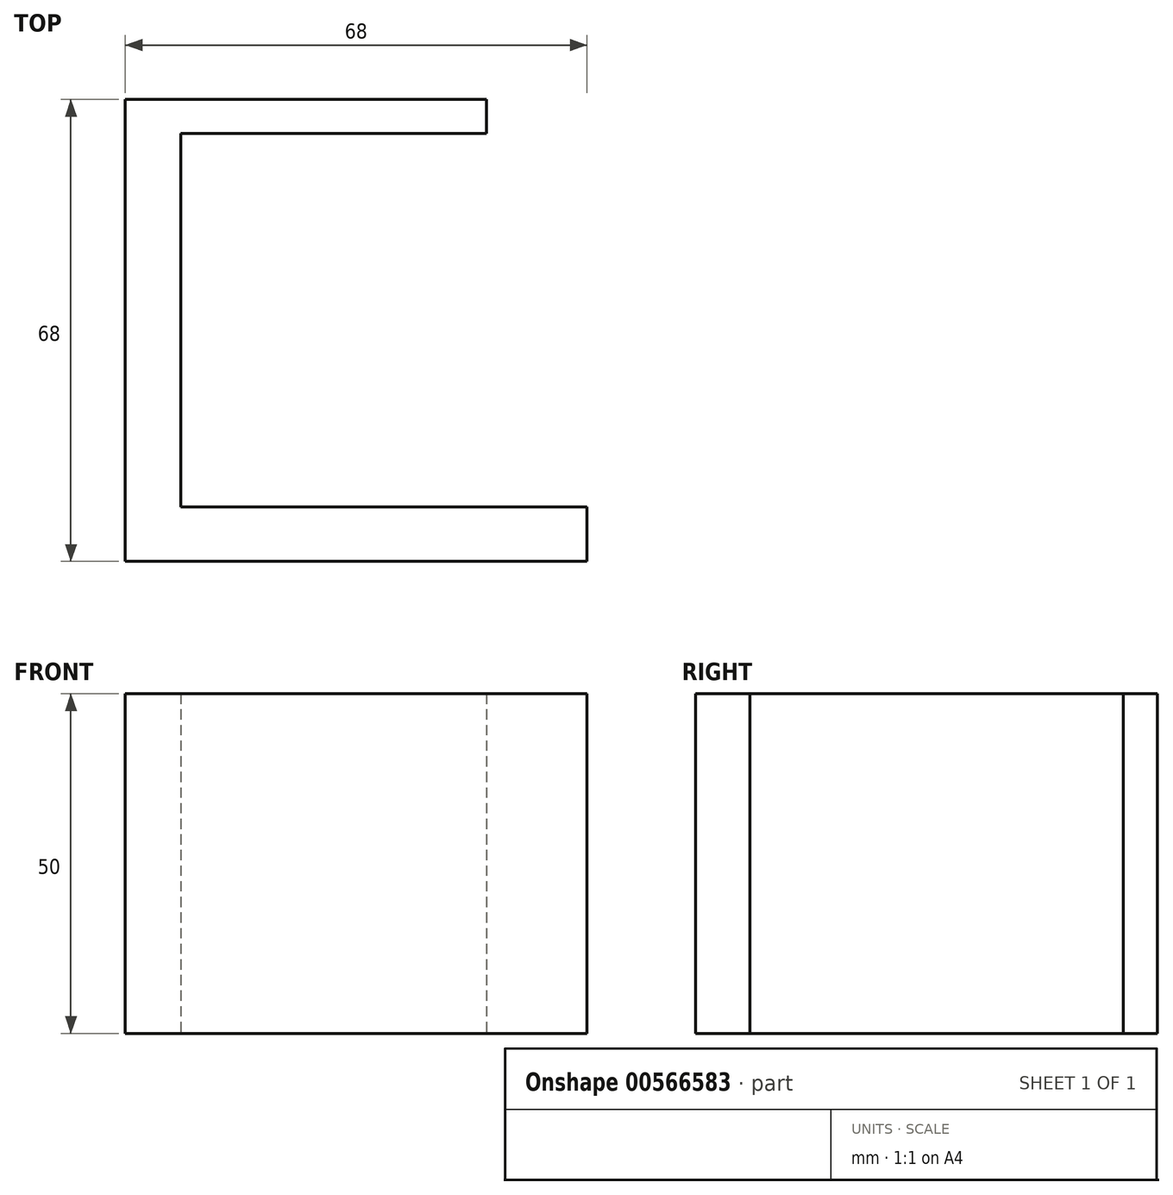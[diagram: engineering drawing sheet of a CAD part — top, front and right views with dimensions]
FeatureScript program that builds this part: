
annotation { "Feature Type Name" : "Feature", "Feature Type Description" : "" }
export const myFeature = defineFeature(function(context is Context, id is Id, definition is map)
    precondition{}
    {
        {
            var Q0;
            Q0=qCreatedBy(makeId("Top.planeOp"),FACE);
            var sketch = newSketch(context, id + "F0", { "sketchPlane" : qUnion([Q0])});
            skLineSegment(sketch, "E0", {"start": v(0, 0) * mm, "end": v(0, -68) * mm});
            skLineSegment(sketch, "E1", {"start": v(0, -68) * mm, "end": v(68, -68) * mm});
            skLineSegment(sketch, "E2", {"start": v(68, -68) * mm, "end": v(68, -60) * mm});
            skLineSegment(sketch, "E3", {"start": v(68, -60) * mm, "end": v(8.18, -60) * mm});
            skLineSegment(sketch, "E4", {"start": v(8.18, -60) * mm, "end": v(8.18, -5) * mm});
            skLineSegment(sketch, "E5", {"start": v(8.18, -5) * mm, "end": v(53.18, -5) * mm});
            skLineSegment(sketch, "E6", {"start": v(53.18, -5) * mm, "end": v(53.18, 0) * mm});
            skLineSegment(sketch, "E7", {"start": v(53.18, 0) * mm, "end": v(0, 0) * mm});
            skSolve(sketch);
        }
        {
            var Q0;
            Q0=makeQuery(id+"F0.imprint","IMPRINT",FACE,{"disambiguationData":[TD([[makeQuery(id+"F0.imprint","IMPRINT",EDGE,{"derivedFrom":sQuery(id+"F0.wireOp",EDGE,"E0")}),1.0]])]});
            extrude(context, id + "F1", {"entities" : qUnion([Q0]), "depth" : 50 * mm, "offsetDistance" : 25 * mm});
        }
    });
